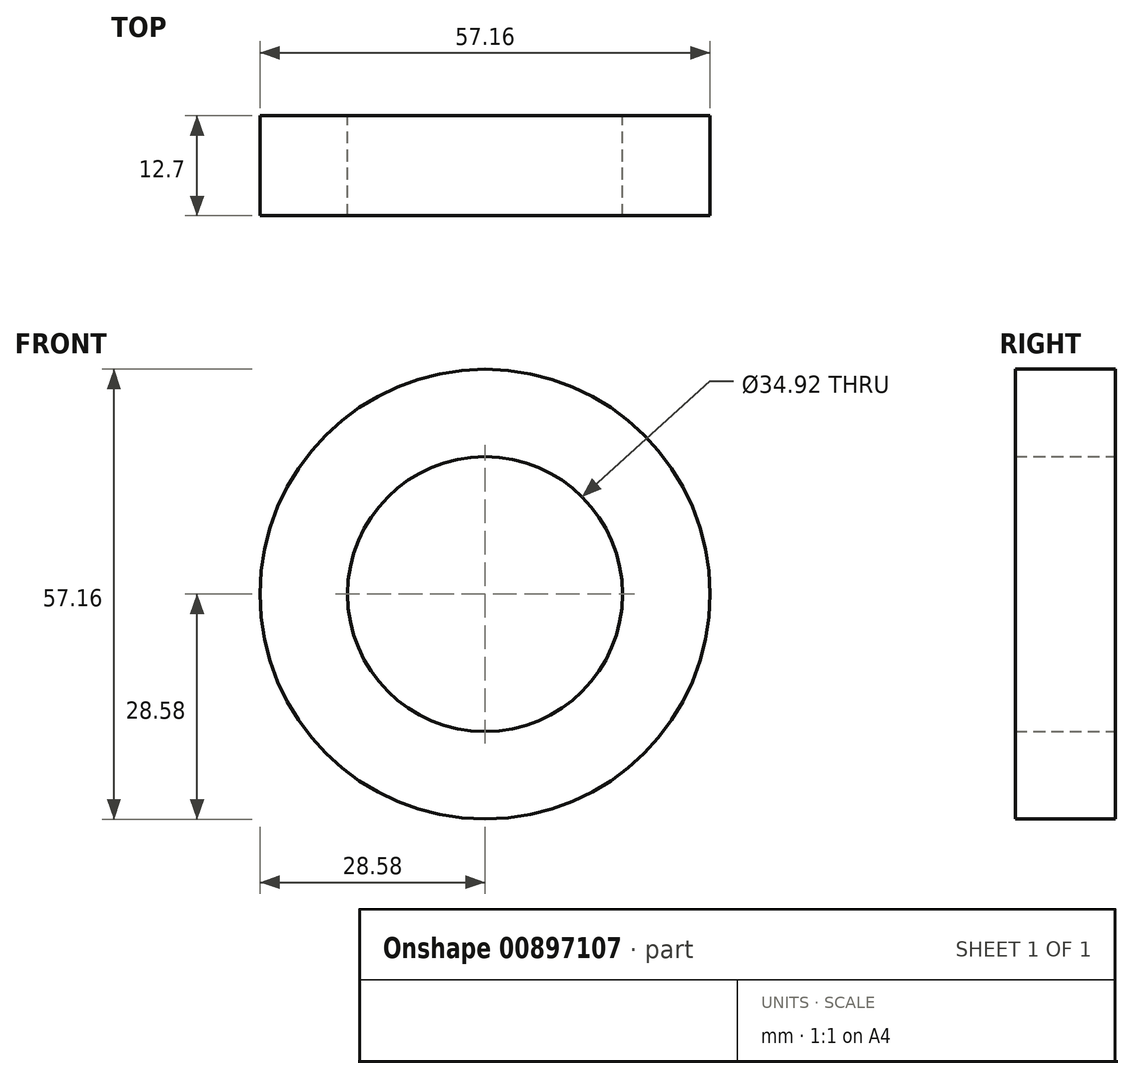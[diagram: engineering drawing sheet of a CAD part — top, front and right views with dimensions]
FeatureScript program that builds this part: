
annotation { "Feature Type Name" : "Feature", "Feature Type Description" : "" }
export const myFeature = defineFeature(function(context is Context, id is Id, definition is map)
    precondition{}
    {
        {
            var Q0;
            Q0=qCreatedBy(makeId("Front.planeOp"),FACE);
            var sketch = newSketch(context, id + "F0", { "sketchPlane" : qUnion([Q0])});
            skCircle(sketch, "E0", {"center": v(0, 0) * mm, "radius": 17.46 * mm});
            skCircle(sketch, "E1", {"center": v(0, 0) * mm, "radius": 28.58 * mm});
            skSolve(sketch);
        }
        {
            var Q0;
            Q0=qSketchRegion(id+"F0",true);
            extrude(context, id + "F1", {"entities" : qUnion([Q0]), "depth" : 12.7 * mm});
        }
    });
